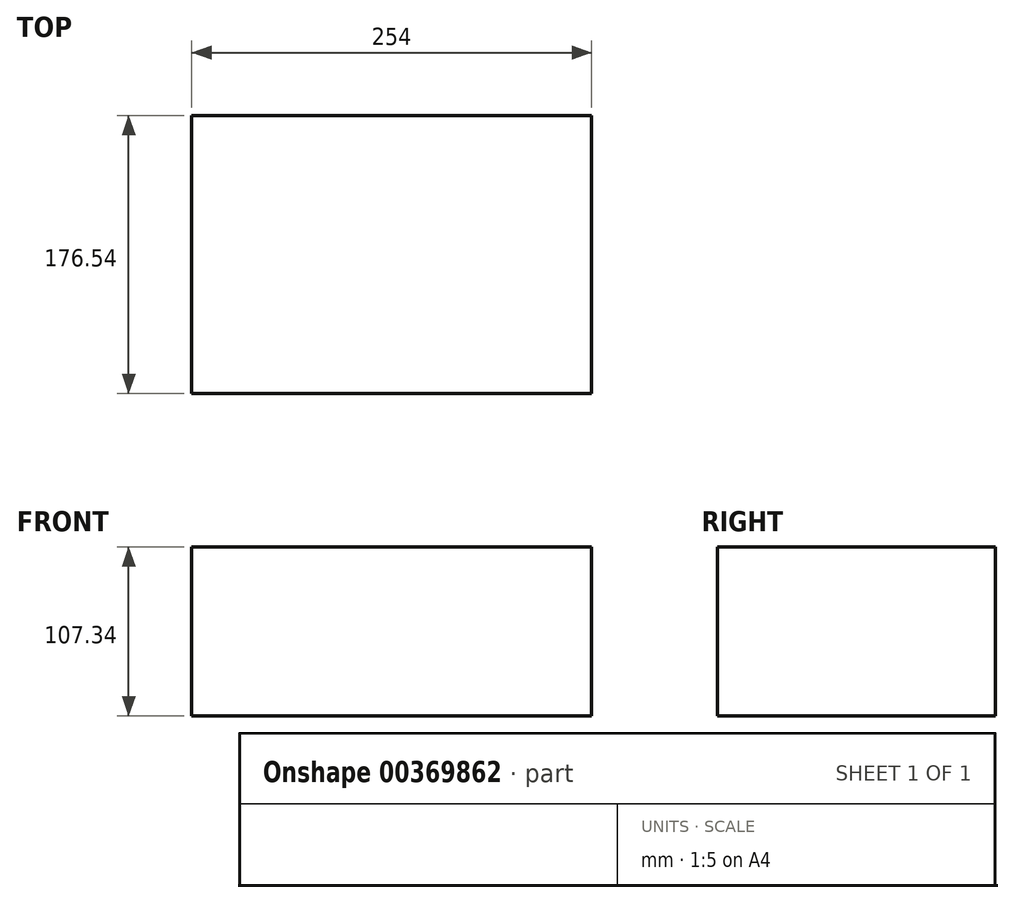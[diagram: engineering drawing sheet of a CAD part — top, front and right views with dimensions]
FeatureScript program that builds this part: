
annotation { "Feature Type Name" : "Feature", "Feature Type Description" : "" }
export const myFeature = defineFeature(function(context is Context, id is Id, definition is map)
    precondition{}
    {
        {
            var Q0;
            Q0=qCreatedBy(makeId("Right.planeOp"),FACE);
            var sketch = newSketch(context, id + "F0", { "sketchPlane" : qUnion([Q0])});
            skLineSegment(sketch, "E0.bottom", {"start": v(88.27, 53.67) * mm, "end": v(-88.27, 53.67) * mm});
            skLineSegment(sketch, "E0.top", {"start": v(88.27, -53.67) * mm, "end": v(-88.27, -53.67) * mm});
            skLineSegment(sketch, "E0.left", {"start": v(88.27, 53.67) * mm, "end": v(88.27, -53.67) * mm});
            skLineSegment(sketch, "E0.right", {"start": v(-88.27, 53.67) * mm, "end": v(-88.27, -53.67) * mm});
            skPoint(sketch, "E0.middle", {"position": v(0, 0) * mm});
            skSolve(sketch);
        }
        {
            var Q0;
            Q0 = qSketchRegion(id + "F0", true);
            extrude(context, id + "F1", {"entities" : qUnion([Q0]), "oppositeDirection" : true, "depth" : 127 * mm});
        }
        {
            var Q0;
            Q0=makeQuery(id+"F1.opExtrude","CAP_FACE",FACE,{"disambiguationData":[OSD([sQuery(id+"F0.wireOp",EDGE,"E0.bottom"),sQuery(id+"F0.wireOp",EDGE,"E0.top"),sQuery(id+"F0.wireOp",EDGE,"E0.left"),sQuery(id+"F0.wireOp",EDGE,"E0.right")])],"isStart":true});
            extrude(context, id + "F2", {"entities" : qUnion([Q0]), "operationType" : NewBodyOperationType.ADD, "depth" : 127 * mm});
        }
    });
